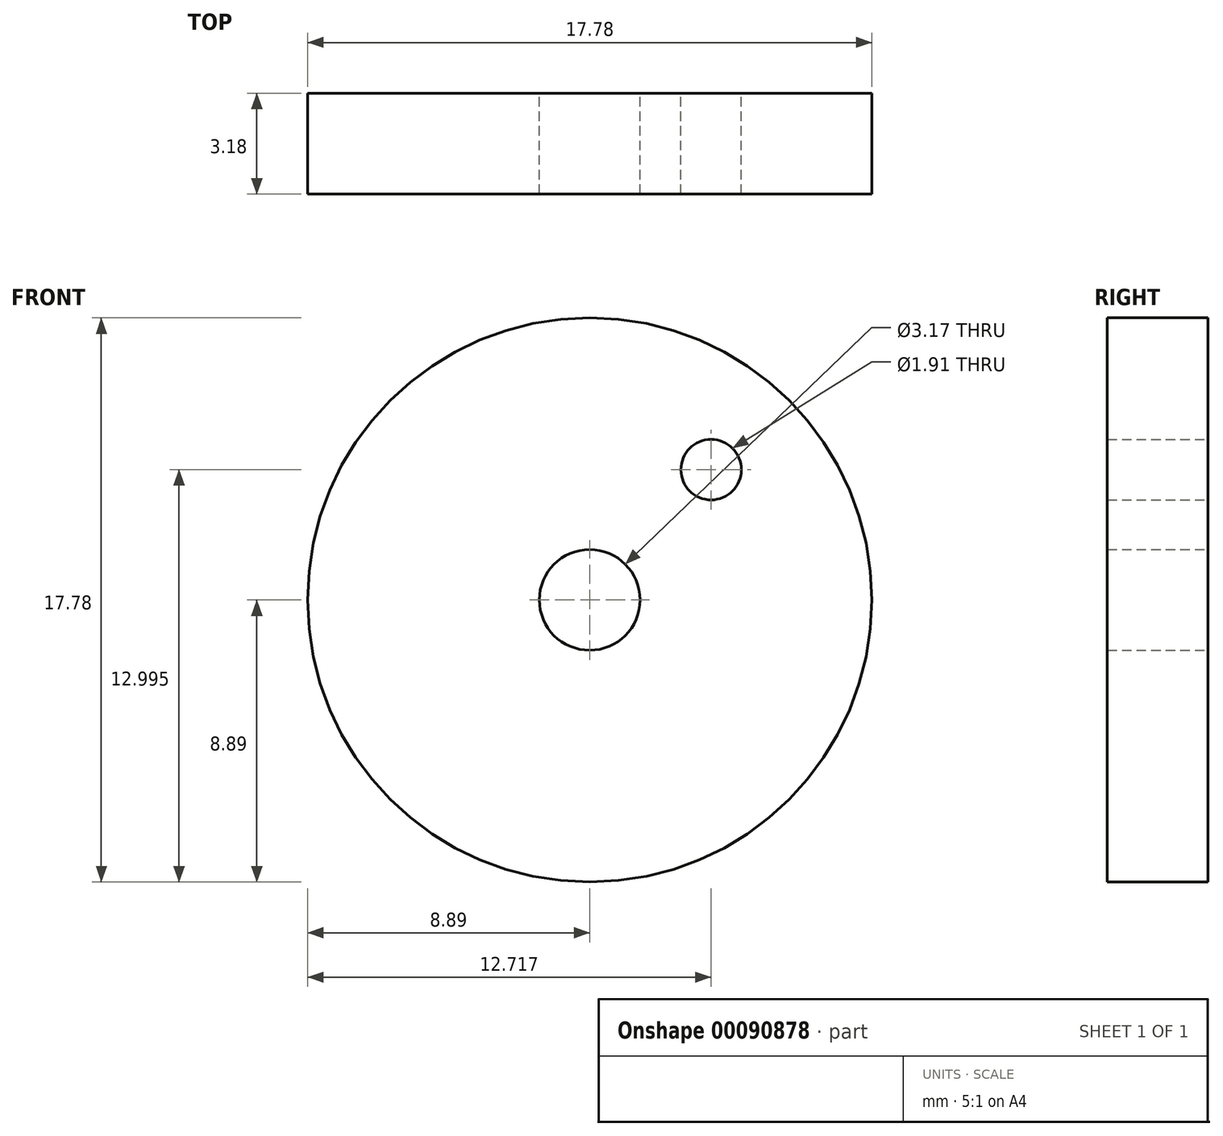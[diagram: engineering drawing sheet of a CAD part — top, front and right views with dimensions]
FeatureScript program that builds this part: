
annotation { "Feature Type Name" : "Feature", "Feature Type Description" : "" }
export const myFeature = defineFeature(function(context is Context, id is Id, definition is map)
    precondition{}
    {
        {
            var Q0;
            Q0=qCreatedBy(makeId("Front.planeOp"),FACE);
            var sketch = newSketch(context, id + "F0", { "sketchPlane" : qUnion([Q0])});
            skCircle(sketch, "E0", {"center": v(0, 0) * mm, "radius": 8.9 * mm});
            skCircle(sketch, "E1", {"center": v(0, 0) * mm, "radius": 1.59 * mm});
            skCircle(sketch, "E2", {"center": v(3.83, 4.1) * mm, "radius": 0.95 * mm});
            skSolve(sketch);
        }
        {
            var Q0;
            Q0 = qSketchRegion(id + "F0", true);
            extrude(context, id + "F1", {"entities" : qUnion([Q0]), "endBound" : BoundingType.SYMMETRIC, "depth" : 3.17 * mm});
        }
    });
